# Revit family: AFX-Irvine-Vanity
name_source: partatom
category: Lighting Fixtures
units: mm (PartAtom-declared; Revit-internal decimal feet)

## family parameters
Cut with Voids When Loaded = No
Host = Face
Light Source = No
Part Type = Normal
Room Calculation Point = No
Round Connector Dimension = Use Diameter
Shared = No

## types (2) — shared parameters
Apparent Load = 0 VA
Assembly Code = D5020200
Canopy Finish = AFX - Black Steel
Colour Rendering Index = 80
Depth = 6 1/2"
Diffuser Finish = AFX - White Acrylic
Height = 12"
Housing Finish = AFX - Black Steel
Keynote = 12500
Manufacturer = AFX Inc
Power Factor = 1
Product Documentation Link = https://www.afxinc.com
Revit File Built By = https://servex-us.com
Sustainability = https://lamprecycle.org
Type Comments = Irvine
URL = https://www.afxinc.com
Voltage = 120 V
Wattage Comments = 15

## per-type parameters (varying)
| type | Default Elevation | Description | Length | Qty |
| IRVV2406LAJUDBK | 48" | Led Vanity - 24"W 6 1/2"D 12"H | 24" | 3 |
| IRVV3206LAJUDBK | 0" | Led Vanity - 33"W x 6 1/2"D x 12"H | 33" | 4 |

note: column(s) folded — value = type name in every type: Model

## geometry (parser evidence)
native form markers: Sweep x6
no freeform markers — native parametric forms only
